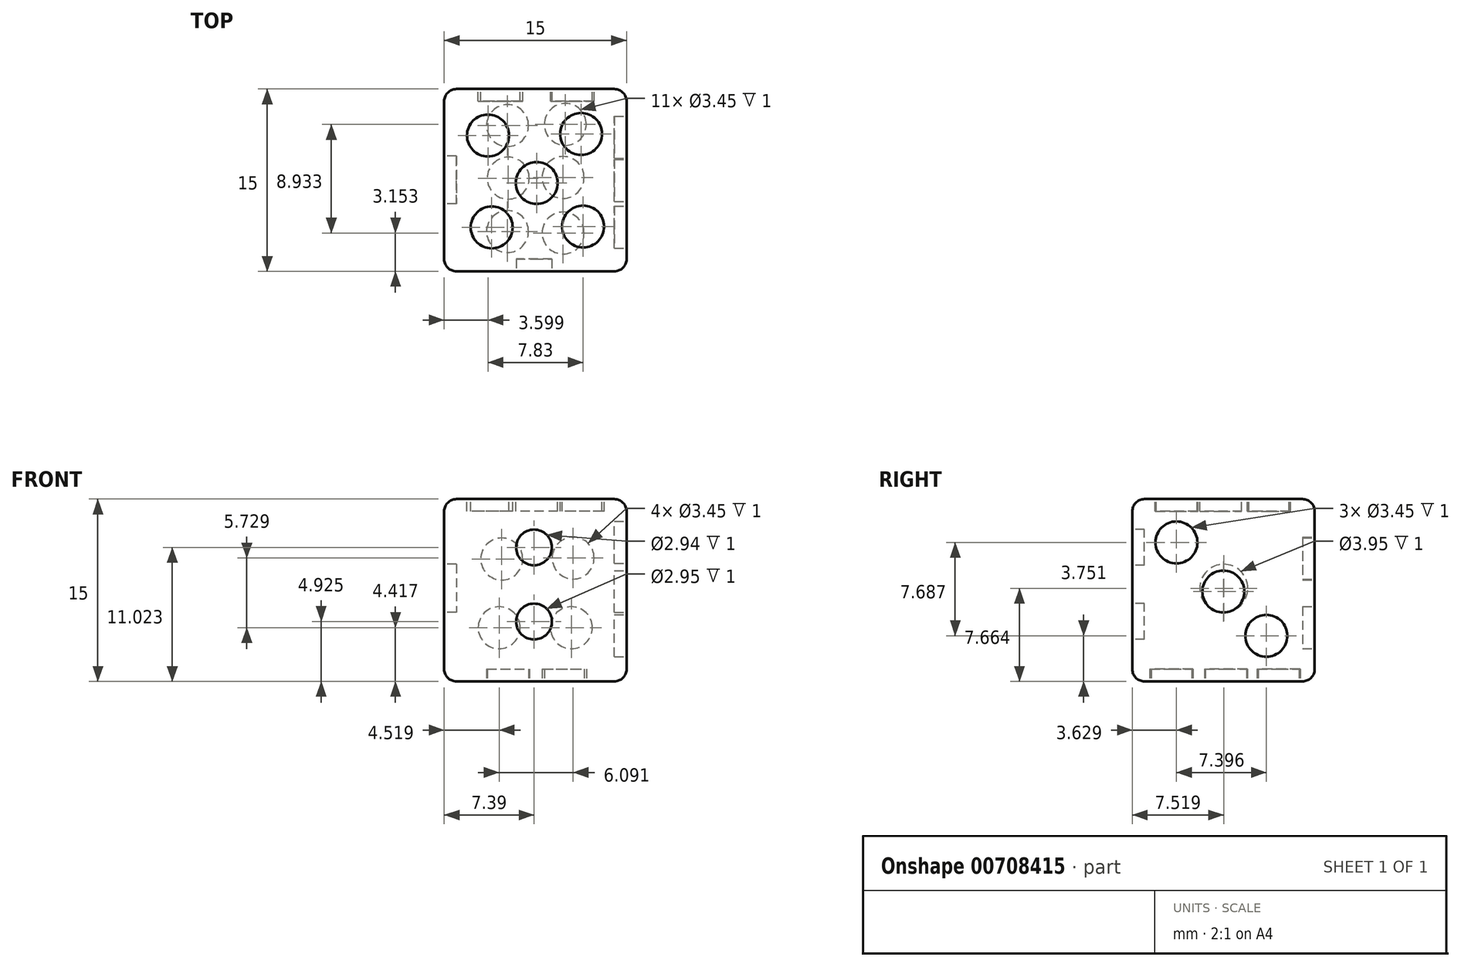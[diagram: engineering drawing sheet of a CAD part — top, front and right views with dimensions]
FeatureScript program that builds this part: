
annotation { "Feature Type Name" : "Feature", "Feature Type Description" : "" }
export const myFeature = defineFeature(function(context is Context, id is Id, definition is map)
    precondition{}
    {
        {
            var Q0;
            Q0=qCreatedBy(makeId("Top.planeOp"),FACE);
            var sketch = newSketch(context, id + "F0", { "sketchPlane" : qUnion([Q0])});
            skLineSegment(sketch, "E0.bottom", {"start": v(0, 0) * mm, "end": v(15, 0) * mm});
            skLineSegment(sketch, "E0.top", {"start": v(0, 15) * mm, "end": v(15, 15) * mm});
            skLineSegment(sketch, "E0.left", {"start": v(0, 0) * mm, "end": v(0, 15) * mm});
            skLineSegment(sketch, "E0.right", {"start": v(15, 0) * mm, "end": v(15, 15) * mm});
            skCircle(sketch, "E1", {"center": v(7.5, 7.77) * mm, "radius": 2.62 * mm});
            skSolve(sketch);
        }
        {
            var Q0;
            Q0=makeQuery(id+"F0.imprint","IMPRINT",FACE,{"disambiguationData":[TD([[makeQuery(id+"F0.imprint","IMPRINT",EDGE,{"derivedFrom":sQuery(id+"F0.wireOp",EDGE,"E1")}),1.0]])]});
            var Q1;
            Q1=makeQuery(id+"F0.imprint","IMPRINT",FACE,{"disambiguationData":[TD([[makeQuery(id+"F0.imprint","IMPRINT",EDGE,{"derivedFrom":sQuery(id+"F0.wireOp",EDGE,"E0.bottom")}),1.0]])]});
            extrude(context, id + "F1", {"entities" : qUnion([Q0, Q1]), "depth" : 15 * mm, "offsetDistance" : 25 * mm});
        }
        {
            var Q0;
            Q0=makeQuery(id+"F1.opExtrude","SWEPT_FACE",FACE,{"disambiguationData":[OSD([sQuery(id+"F0.wireOp",EDGE,"E0.bottom")])]});
            var sketch = newSketch(context, id + "F2", { "sketchPlane" : qUnion([Q0])});
            skCircle(sketch, "E2", {"center": v(7.4, 11.02) * mm, "radius": 1.47 * mm});
            skCircle(sketch, "E3", {"center": v(7.4, 4.93) * mm, "radius": 1.47 * mm});
            skSolve(sketch);
        }
        {
            var Q0;
            Q0=makeQuery(id+"F1.opExtrude","SWEPT_FACE",FACE,{"disambiguationData":[OSD([sQuery(id+"F0.wireOp",EDGE,"E0.right")])]});
            var sketch = newSketch(context, id + "F3", { "sketchPlane" : qUnion([Q0])});
            skCircle(sketch, "E4", {"center": v(7.48, 7.39) * mm, "radius": 1.72 * mm});
            skCircle(sketch, "E5", {"center": v(3.63, 11.44) * mm, "radius": 1.72 * mm});
            skCircle(sketch, "E6", {"center": v(11.03, 3.75) * mm, "radius": 1.72 * mm});
            skSolve(sketch);
        }
        {
            var Q0;
            Q0=makeQuery(id+"F1.opExtrude","SWEPT_FACE",FACE,{"disambiguationData":[OSD([sQuery(id+"F0.wireOp",EDGE,"E0.top")])]});
            var sketch = newSketch(context, id + "F4", { "sketchPlane" : qUnion([Q0])});
            skCircle(sketch, "E7", {"center": v(-10.6, 10.15) * mm, "radius": 1.72 * mm});
            skCircle(sketch, "E8", {"center": v(-4.52, 4.42) * mm, "radius": 1.72 * mm});
            skCircle(sketch, "E9", {"center": v(-4.74, 10.07) * mm, "radius": 1.72 * mm});
            skCircle(sketch, "E10", {"center": v(-10.46, 4.42) * mm, "radius": 1.72 * mm});
            skSolve(sketch);
        }
        {
            var Q0;
            Q0=makeQuery(id+"F1.opExtrude","SWEPT_FACE",FACE,{"disambiguationData":[OSD([sQuery(id+"F0.wireOp",EDGE,"E0.left")])]});
            var sketch = newSketch(context, id + "F5", { "sketchPlane" : qUnion([Q0])});
            skCircle(sketch, "E11", {"center": v(-7.52, 7.66) * mm, "radius": 1.98 * mm});
            skSolve(sketch);
        }
        {
            var Q0;
            Q0=makeQuery(id+"F1.opExtrude","CAP_FACE",FACE,{"disambiguationData":[OSD([sQuery(id+"F0.wireOp",EDGE,"E0.bottom"),sQuery(id+"F0.wireOp",EDGE,"E0.top"),sQuery(id+"F0.wireOp",EDGE,"E0.left"),sQuery(id+"F0.wireOp",EDGE,"E0.right")])],"isStart":false});
            var sketch = newSketch(context, id + "F6", { "sketchPlane" : qUnion([Q0])});
            skCircle(sketch, "E12", {"center": v(7.6, 7.27) * mm, "radius": 1.72 * mm});
            skCircle(sketch, "E13", {"center": v(3.6, 11.18) * mm, "radius": 1.72 * mm});
            skCircle(sketch, "E14", {"center": v(3.9, 3.6) * mm, "radius": 1.72 * mm});
            skCircle(sketch, "E15", {"center": v(11.43, 3.69) * mm, "radius": 1.72 * mm});
            skCircle(sketch, "E16", {"center": v(11.26, 11.3) * mm, "radius": 1.72 * mm});
            skSolve(sketch);
        }
        {
            var Q0;
            Q0=makeQuery(id+"F1.opExtrude","CAP_FACE",FACE,{"disambiguationData":[OSD([sQuery(id+"F0.wireOp",EDGE,"E0.bottom"),sQuery(id+"F0.wireOp",EDGE,"E0.top"),sQuery(id+"F0.wireOp",EDGE,"E0.left"),sQuery(id+"F0.wireOp",EDGE,"E0.right")])],"isStart":true});
            var sketch = newSketch(context, id + "F7", { "sketchPlane" : qUnion([Q0])});
            skCircle(sketch, "E17", {"center": v(5.21, -3.27) * mm, "radius": 1.72 * mm});
            skCircle(sketch, "E18", {"center": v(5.27, -7.67) * mm, "radius": 1.72 * mm});
            skCircle(sketch, "E19", {"center": v(5.21, -12) * mm, "radius": 1.72 * mm});
            skCircle(sketch, "E20", {"center": v(9.78, -3.15) * mm, "radius": 1.72 * mm});
            skCircle(sketch, "E21", {"center": v(9.78, -7.73) * mm, "radius": 1.72 * mm});
            skCircle(sketch, "E22", {"center": v(9.97, -12.09) * mm, "radius": 1.72 * mm});
            skSolve(sketch);
        }
        {
            var Q0;
            Q0=makeQuery(id+"F2.imprint","IMPRINT",FACE,{"disambiguationData":[TD([[makeQuery(id+"F2.imprint","IMPRINT",EDGE,{"derivedFrom":sQuery(id+"F2.wireOp",EDGE,"E3")}),1.0]])]});
            var Q1;
            Q1=makeQuery(id+"F2.imprint","IMPRINT",FACE,{"disambiguationData":[TD([[makeQuery(id+"F2.imprint","IMPRINT",EDGE,{"derivedFrom":sQuery(id+"F2.wireOp",EDGE,"E2")}),1.0]])]});
            extrude(context, id + "F8", {"entities" : qUnion([Q0, Q1]), "operationType" : NewBodyOperationType.REMOVE, "oppositeDirection" : true, "depth" : 1 * mm, "offsetDistance" : 25 * mm});
        }
        {
            var Q0;
            Q0=makeQuery(id+"F5.imprint","IMPRINT",FACE,{"disambiguationData":[TD([[makeQuery(id+"F5.imprint","IMPRINT",EDGE,{"derivedFrom":sQuery(id+"F5.wireOp",EDGE,"E11")}),1.0]])]});
            extrude(context, id + "F9", {"entities" : qUnion([Q0]), "operationType" : NewBodyOperationType.REMOVE, "oppositeDirection" : true, "depth" : 1 * mm, "offsetDistance" : 25 * mm});
        }
        {
            var Q0;
            Q0=makeQuery(id+"F4.imprint","IMPRINT",FACE,{"disambiguationData":[TD([[makeQuery(id+"F4.imprint","IMPRINT",EDGE,{"derivedFrom":sQuery(id+"F4.wireOp",EDGE,"E8")}),1.0]])]});
            var Q1;
            Q1=makeQuery(id+"F4.imprint","IMPRINT",FACE,{"disambiguationData":[TD([[makeQuery(id+"F4.imprint","IMPRINT",EDGE,{"derivedFrom":sQuery(id+"F4.wireOp",EDGE,"E7")}),1.0]])]});
            var Q2;
            Q2=makeQuery(id+"F4.imprint","IMPRINT",FACE,{"disambiguationData":[TD([[makeQuery(id+"F4.imprint","IMPRINT",EDGE,{"derivedFrom":sQuery(id+"F4.wireOp",EDGE,"E10")}),1.0]])]});
            var Q3;
            Q3=makeQuery(id+"F4.imprint","IMPRINT",FACE,{"disambiguationData":[TD([[makeQuery(id+"F4.imprint","IMPRINT",EDGE,{"derivedFrom":sQuery(id+"F4.wireOp",EDGE,"E9")}),1.0]])]});
            extrude(context, id + "F10", {"entities" : qUnion([Q0, Q1, Q2, Q3]), "operationType" : NewBodyOperationType.REMOVE, "oppositeDirection" : true, "depth" : 1 * mm, "offsetDistance" : 25 * mm});
        }
        {
            var Q0;
            Q0=makeQuery(id+"F3.imprint","IMPRINT",FACE,{"disambiguationData":[TD([[makeQuery(id+"F3.imprint","IMPRINT",EDGE,{"derivedFrom":sQuery(id+"F3.wireOp",EDGE,"E4")}),1.0]])]});
            var Q1;
            Q1=makeQuery(id+"F3.imprint","IMPRINT",FACE,{"disambiguationData":[TD([[makeQuery(id+"F3.imprint","IMPRINT",EDGE,{"derivedFrom":sQuery(id+"F3.wireOp",EDGE,"E5")}),1.0]])]});
            var Q2;
            Q2=makeQuery(id+"F3.imprint","IMPRINT",FACE,{"disambiguationData":[TD([[makeQuery(id+"F3.imprint","IMPRINT",EDGE,{"derivedFrom":sQuery(id+"F3.wireOp",EDGE,"E6")}),1.0]])]});
            extrude(context, id + "F11", {"entities" : qUnion([Q0, Q1, Q2]), "operationType" : NewBodyOperationType.REMOVE, "oppositeDirection" : true, "depth" : 1 * mm, "offsetDistance" : 25 * mm});
        }
        {
            var Q0;
            Q0=makeQuery(id+"F7.imprint","IMPRINT",FACE,{"disambiguationData":[TD([[makeQuery(id+"F7.imprint","IMPRINT",EDGE,{"derivedFrom":sQuery(id+"F7.wireOp",EDGE,"E18")}),1.0]])]});
            var Q1;
            Q1=makeQuery(id+"F7.imprint","IMPRINT",FACE,{"disambiguationData":[TD([[makeQuery(id+"F7.imprint","IMPRINT",EDGE,{"derivedFrom":sQuery(id+"F7.wireOp",EDGE,"E17")}),1.0]])]});
            var Q2;
            Q2=makeQuery(id+"F7.imprint","IMPRINT",FACE,{"disambiguationData":[TD([[makeQuery(id+"F7.imprint","IMPRINT",EDGE,{"derivedFrom":sQuery(id+"F7.wireOp",EDGE,"E22")}),1.0]])]});
            var Q3;
            Q3=makeQuery(id+"F7.imprint","IMPRINT",FACE,{"disambiguationData":[TD([[makeQuery(id+"F7.imprint","IMPRINT",EDGE,{"derivedFrom":sQuery(id+"F7.wireOp",EDGE,"E21")}),1.0]])]});
            var Q4;
            Q4=makeQuery(id+"F7.imprint","IMPRINT",FACE,{"disambiguationData":[TD([[makeQuery(id+"F7.imprint","IMPRINT",EDGE,{"derivedFrom":sQuery(id+"F7.wireOp",EDGE,"E20")}),1.0]])]});
            var Q5;
            Q5=makeQuery(id+"F7.imprint","IMPRINT",FACE,{"disambiguationData":[TD([[makeQuery(id+"F7.imprint","IMPRINT",EDGE,{"derivedFrom":sQuery(id+"F7.wireOp",EDGE,"E19")}),1.0]])]});
            extrude(context, id + "F12", {"entities" : qUnion([Q0, Q1, Q2, Q3, Q4, Q5]), "operationType" : NewBodyOperationType.REMOVE, "oppositeDirection" : true, "depth" : 1 * mm, "offsetDistance" : 25 * mm});
        }
        {
            var Q0;
            Q0=makeQuery(id+"F6.imprint","IMPRINT",FACE,{"disambiguationData":[TD([[makeQuery(id+"F6.imprint","IMPRINT",EDGE,{"derivedFrom":sQuery(id+"F6.wireOp",EDGE,"E12")}),1.0]])]});
            var Q1;
            Q1=makeQuery(id+"F6.imprint","IMPRINT",FACE,{"disambiguationData":[TD([[makeQuery(id+"F6.imprint","IMPRINT",EDGE,{"derivedFrom":sQuery(id+"F6.wireOp",EDGE,"E15")}),1.0]])]});
            var Q2;
            Q2=makeQuery(id+"F6.imprint","IMPRINT",FACE,{"disambiguationData":[TD([[makeQuery(id+"F6.imprint","IMPRINT",EDGE,{"derivedFrom":sQuery(id+"F6.wireOp",EDGE,"E16")}),1.0]])]});
            var Q3;
            Q3=makeQuery(id+"F6.imprint","IMPRINT",FACE,{"disambiguationData":[TD([[makeQuery(id+"F6.imprint","IMPRINT",EDGE,{"derivedFrom":sQuery(id+"F6.wireOp",EDGE,"E13")}),1.0]])]});
            var Q4;
            Q4=makeQuery(id+"F6.imprint","IMPRINT",FACE,{"disambiguationData":[TD([[makeQuery(id+"F6.imprint","IMPRINT",EDGE,{"derivedFrom":sQuery(id+"F6.wireOp",EDGE,"E14")}),1.0]])]});
            extrude(context, id + "F13", {"entities" : qUnion([Q0, Q1, Q2, Q3, Q4]), "operationType" : NewBodyOperationType.REMOVE, "oppositeDirection" : true, "depth" : 1 * mm, "offsetDistance" : 25 * mm});
        }
        {
            var Q0;
            Q0=makeQuery(id+"F1.opExtrude","CAP_EDGE",EDGE,{"disambiguationData":[OSD([sQuery(id+"F0.wireOp",EDGE,"E0.right")])],"isStart":true});
            var Q1;
            Q1=makeQuery(id+"F1.opExtrude","CAP_EDGE",EDGE,{"disambiguationData":[OSD([sQuery(id+"F0.wireOp",EDGE,"E0.top")])],"isStart":true});
            var Q2;
            Q2=makeQuery(id+"F1.opExtrude","SWEPT_EDGE",EDGE,{"disambiguationData":[OSD([sQuery(id+"F0.wireOp",EDGE,"E0.top"),sQuery(id+"F0.wireOp",EDGE,"E0.right")])]});
            var Q3;
            Q3=makeQuery(id+"F1.opExtrude","CAP_EDGE",EDGE,{"disambiguationData":[OSD([sQuery(id+"F0.wireOp",EDGE,"E0.bottom")])],"isStart":true});
            var Q4;
            Q4=makeQuery(id+"F1.opExtrude","CAP_EDGE",EDGE,{"disambiguationData":[OSD([sQuery(id+"F0.wireOp",EDGE,"E0.left")])],"isStart":true});
            var Q5;
            Q5=makeQuery(id+"F1.opExtrude","SWEPT_EDGE",EDGE,{"disambiguationData":[OSD([sQuery(id+"F0.wireOp",EDGE,"E0.top"),sQuery(id+"F0.wireOp",EDGE,"E0.left")])]});
            var Q6;
            Q6=makeQuery(id+"F1.opExtrude","CAP_EDGE",EDGE,{"disambiguationData":[OSD([sQuery(id+"F0.wireOp",EDGE,"E0.left")])],"isStart":false});
            var Q7;
            Q7=makeQuery(id+"F1.opExtrude","SWEPT_EDGE",EDGE,{"disambiguationData":[OSD([sQuery(id+"F0.wireOp",EDGE,"E0.bottom"),sQuery(id+"F0.wireOp",EDGE,"E0.left")])]});
            var Q8;
            Q8=makeQuery(id+"F1.opExtrude","CAP_EDGE",EDGE,{"disambiguationData":[OSD([sQuery(id+"F0.wireOp",EDGE,"E0.bottom")])],"isStart":false});
            var Q9;
            Q9=makeQuery(id+"F1.opExtrude","SWEPT_EDGE",EDGE,{"disambiguationData":[OSD([sQuery(id+"F0.wireOp",EDGE,"E0.bottom"),sQuery(id+"F0.wireOp",EDGE,"E0.right")])]});
            var Q10;
            Q10=makeQuery(id+"F1.opExtrude","CAP_EDGE",EDGE,{"disambiguationData":[OSD([sQuery(id+"F0.wireOp",EDGE,"E0.right")])],"isStart":false});
            var Q11;
            Q11=makeQuery(id+"F1.opExtrude","CAP_EDGE",EDGE,{"disambiguationData":[OSD([sQuery(id+"F0.wireOp",EDGE,"E0.top")])],"isStart":false});
            fillet(context, id + "F14", {"entities" : qUnion([Q0, Q1, Q2, Q3, Q4, Q5, Q6, Q7, Q8, Q9, Q10, Q11]), "radius" : 1 * mm, "tangentPropagation" : true, "allowEdgeOverflow" : false});
        }
    });
